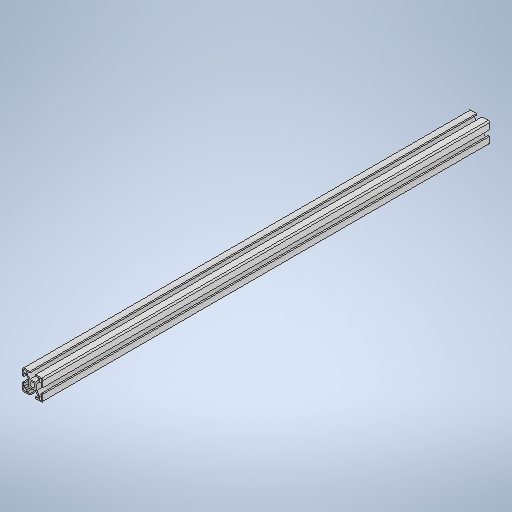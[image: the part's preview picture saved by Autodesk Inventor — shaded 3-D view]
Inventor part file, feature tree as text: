
AUTODESK INVENTOR PART (.ipt)
format: ipt  version: 2025 (Build 290162000, 162)  size: 314,368 bytes
history: native  units: in
note: dims shown in document units (in); Inventor stores cm internally (conversion verified against a paired STEP export)
features: extrude x1, sketch x1
ambient origin geometry x8: Origin, YZ Plane, XZ Plane, XY Plane, X Axis, Y Axis, Z Axis, Center Point
bodies: Solid1 (feature_tree)
feature tree (2):
  extrude  "Extrusion1"  Depth=25.5906in
  sketch  "Sketch1"  dims[d6=25.5906in d7=0.0in d8=0.1969in d9=0.0344in]
